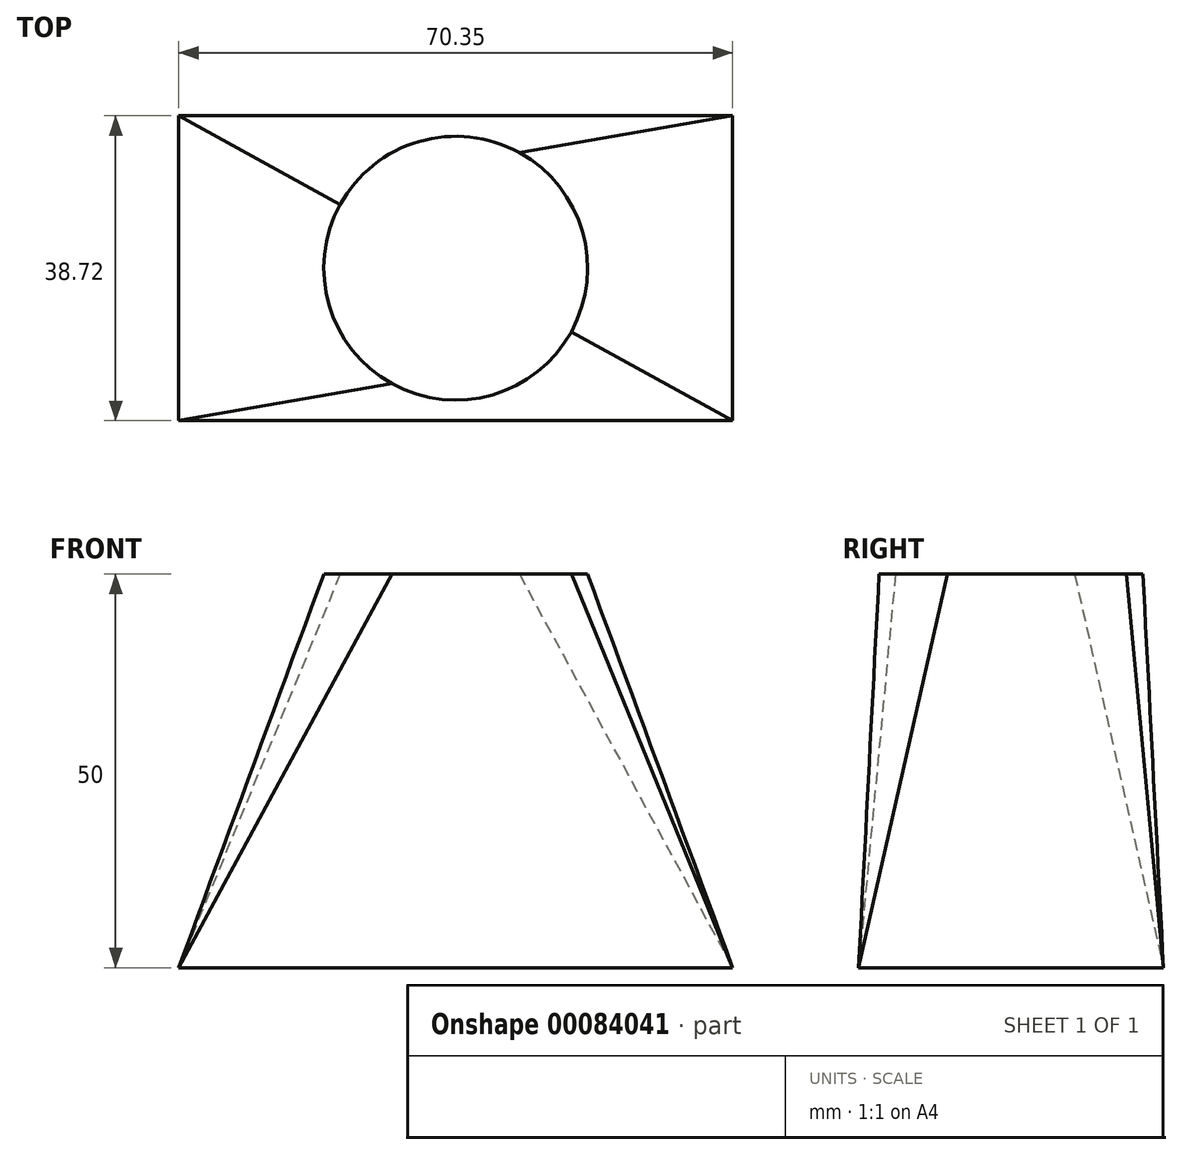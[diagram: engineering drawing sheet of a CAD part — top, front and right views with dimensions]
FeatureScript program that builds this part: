
annotation { "Feature Type Name" : "Feature", "Feature Type Description" : "" }
export const myFeature = defineFeature(function(context is Context, id is Id, definition is map)
    precondition{}
    {
        {
            var Q0;
            Q0=qCreatedBy(makeId("Top.planeOp"),FACE);
            cPlane(context, id + "F0", {"entities" : qUnion([Q0]), "cplaneType" : CPlaneType.OFFSET, "offset" : 50 * mm, "width" : 150 * mm, "height" : 150 * mm});
        }
        {
            var Q0;
            Q0=qCreatedBy(makeId("Top.planeOp"),FACE);
            var sketch = newSketch(context, id + "F1", { "sketchPlane" : qUnion([Q0])});
            skLineSegment(sketch, "E0.bottom", {"start": v(-65.35, -17.43) * mm, "end": v(5, -17.43) * mm});
            skLineSegment(sketch, "E0.top", {"start": v(-65.35, -56.15) * mm, "end": v(5, -56.15) * mm});
            skLineSegment(sketch, "E0.left", {"start": v(-65.35, -17.43) * mm, "end": v(-65.35, -56.15) * mm});
            skLineSegment(sketch, "E0.right", {"start": v(5, -17.43) * mm, "end": v(5, -56.15) * mm});
            skPoint(sketch, "E0.middle", {"position": v(-30.17, -36.79) * mm});
            skLineSegment(sketch, "E1.bottom", {"start": v(46.45, 17.43) * mm, "end": v(-3.55, 17.43) * mm});
            skLineSegment(sketch, "E1.top", {"start": v(46.45, 67.43) * mm, "end": v(-3.55, 67.43) * mm});
            skLineSegment(sketch, "E1.left", {"start": v(46.45, 17.43) * mm, "end": v(46.45, 67.43) * mm});
            skLineSegment(sketch, "E1.right", {"start": v(-3.55, 17.43) * mm, "end": v(-3.55, 67.43) * mm});
            skPoint(sketch, "E1.middle", {"position": v(21.45, 42.43) * mm});
            skSolve(sketch);
        }
        {
            var Q0;
            Q0=qCreatedBy(id+"F0.planeOp",FACE);
            var sketch = newSketch(context, id + "F2", { "sketchPlane" : qUnion([Q0])});
            skPoint(sketch, "E2.0", {"position": v(-30.17, -36.79) * mm});
            skCircle(sketch, "E3", {"center": v(-30.17, -36.79) * mm, "radius": 16.75 * mm});
            skPoint(sketch, "E4.0", {"position": v(21.45, 42.43) * mm});
            skCircle(sketch, "E5.cCircle", {"center": v(21.45, 42.43) * mm, "radius": 17.89 * mm, "construction": true});
            skLineSegment(sketch, "E5.0", {"start": v(39.34, 35.02) * mm, "end": v(28.86, 24.54) * mm});
            skLineSegment(sketch, "E5.1", {"start": v(28.86, 24.54) * mm, "end": v(14.04, 24.54) * mm});
            skLineSegment(sketch, "E5.2", {"start": v(14.04, 24.54) * mm, "end": v(3.56, 35.02) * mm});
            skLineSegment(sketch, "E5.3", {"start": v(3.56, 35.02) * mm, "end": v(3.56, 49.84) * mm});
            skLineSegment(sketch, "E5.4", {"start": v(3.56, 49.84) * mm, "end": v(14.04, 60.31) * mm});
            skLineSegment(sketch, "E5.5", {"start": v(14.04, 60.31) * mm, "end": v(28.86, 60.31) * mm});
            skLineSegment(sketch, "E5.6", {"start": v(28.86, 60.31) * mm, "end": v(39.34, 49.84) * mm});
            skLineSegment(sketch, "E5.7", {"start": v(39.34, 49.84) * mm, "end": v(39.34, 35.02) * mm});
            skPoint(sketch, "E5.0.midPoint", {"position": v(34.1, 29.78) * mm});
            skSolve(sketch);
        }
        {
            var Q0;
            Q0=makeQuery(id+"F2.imprint","IMPRINT",FACE,{"disambiguationData":[TD([[makeQuery(id+"F2.imprint","IMPRINT",EDGE,{"derivedFrom":sQuery(id+"F2.wireOp",EDGE,"E3")}),1.0]])]});
            var Q1;
            Q1=makeQuery(id+"F1.imprint","IMPRINT",FACE,{"disambiguationData":[TD([[makeQuery(id+"F1.imprint","IMPRINT",EDGE,{"derivedFrom":sQuery(id+"F1.wireOp",EDGE,"E0.bottom")}),-1.0]])]});
            loft(context, id + "F3", {"sheetProfilesArray" : [{ "sheetProfileEntities" : qUnion([Q0]) }, { "sheetProfileEntities" : qUnion([Q1]) }]});
        }
        {
            var Q0;
            Q0=sQuery(id+"F2.wireOp",EDGE,"E5.3");
            var Q1;
            Q1=sQuery(id+"F1.wireOp",EDGE,"E1.right");
            loft(context, id + "F4", {"bodyType" : ExtendedToolBodyType.SURFACE, "wireProfilesArray" : [{ "wireProfileEntities" : qUnion([Q0]) }, { "wireProfileEntities" : qUnion([Q1]) }]});
        }
        {
            var Q0;
            Q0=sQuery(id+"F2.wireOp",EDGE,"E5.2");
            var Q1;
            Q1=sQuery(id+"F1.wireOp",VERTEX,"E1.bottom.end");
            loft(context, id + "F5", {"bodyType" : ExtendedToolBodyType.SURFACE, "wireProfilesArray" : [{ "wireProfileEntities" : qUnion([Q0]) }, { "wireProfileEntities" : qUnion([Q1]) }]});
        }
        {
            var Q0;
            Q0=sQuery(id+"F2.wireOp",EDGE,"E5.1");
            var Q1;
            Q1=sQuery(id+"F1.wireOp",EDGE,"E1.bottom");
            loft(context, id + "F6", {"bodyType" : ExtendedToolBodyType.SURFACE, "wireProfilesArray" : [{ "wireProfileEntities" : qUnion([Q0]) }, { "wireProfileEntities" : qUnion([Q1]) }]});
        }
        {
            var Q0;
            Q0=sQuery(id+"F2.wireOp",EDGE,"E5.0");
            var Q1;
            Q1=sQuery(id+"F1.wireOp",VERTEX,"E1.left.start");
            loft(context, id + "F7", {"bodyType" : ExtendedToolBodyType.SURFACE, "wireProfilesArray" : [{ "wireProfileEntities" : qUnion([Q0]) }, { "wireProfileEntities" : qUnion([Q1]) }]});
        }
        {
            var Q0;
            Q0=sQuery(id+"F2.wireOp",EDGE,"E5.7");
            var Q1;
            Q1=sQuery(id+"F1.wireOp",EDGE,"E1.left");
            loft(context, id + "F8", {"bodyType" : ExtendedToolBodyType.SURFACE, "wireProfilesArray" : [{ "wireProfileEntities" : qUnion([Q0]) }, { "wireProfileEntities" : qUnion([Q1]) }]});
        }
        {
            var Q0;
            Q0=sQuery(id+"F1.wireOp",VERTEX,"E1.top.start");
            var Q1;
            Q1=sQuery(id+"F2.wireOp",EDGE,"E5.6");
            var Q2;
            Q2=sQuery(id+"F1.wireOp",VERTEX,"E1.top.start");
            loft(context, id + "F9", {"bodyType" : ExtendedToolBodyType.SURFACE, "sheetProfilesArray" : [{ "sheetProfileEntities" : qUnion([Q0]) }], "wireProfilesArray" : [{ "wireProfileEntities" : qUnion([Q1]) }, { "wireProfileEntities" : qUnion([Q2]) }]});
        }
        {
            var Q0;
            Q0=sQuery(id+"F2.wireOp",EDGE,"E5.5");
            var Q1;
            Q1=sQuery(id+"F1.wireOp",EDGE,"E1.top");
            loft(context, id + "F10", {"bodyType" : ExtendedToolBodyType.SURFACE, "wireProfilesArray" : [{ "wireProfileEntities" : qUnion([Q0]) }, { "wireProfileEntities" : qUnion([Q1]) }]});
        }
        {
            var Q0;
            Q0=sQuery(id+"F1.wireOp",VERTEX,"E1.top.end");
            var Q1;
            Q1=sQuery(id+"F2.wireOp",EDGE,"E5.4");
            loft(context, id + "F11", {"bodyType" : ExtendedToolBodyType.SURFACE, "wireProfilesArray" : [{ "wireProfileEntities" : qUnion([Q0]) }, { "wireProfileEntities" : qUnion([Q1]) }]});
        }
    });
